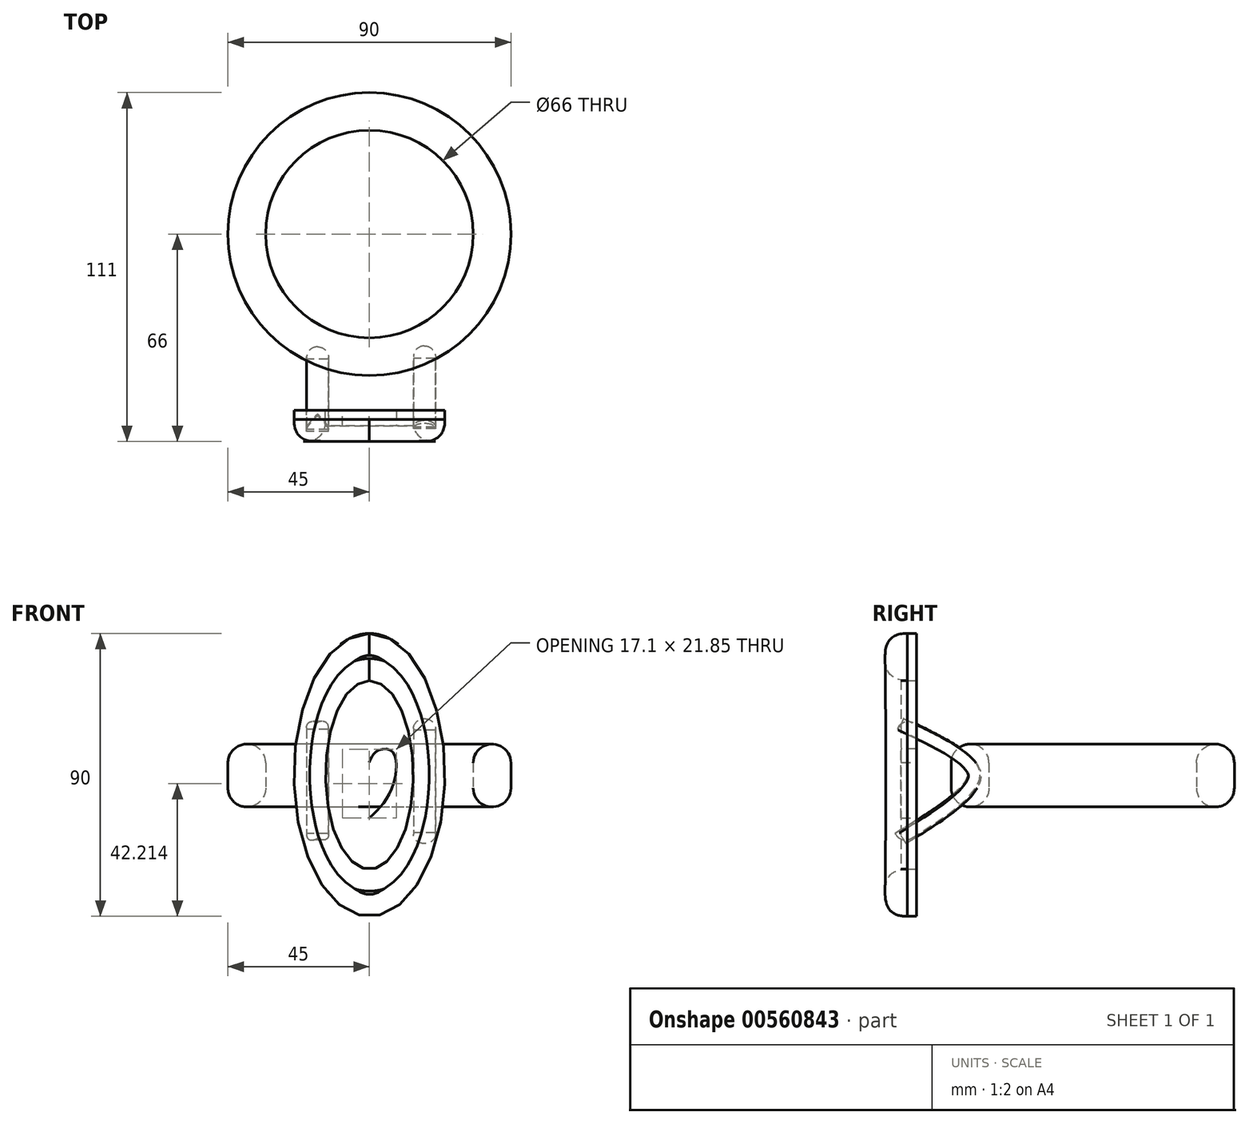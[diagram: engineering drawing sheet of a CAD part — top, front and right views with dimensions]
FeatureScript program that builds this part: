
annotation { "Feature Type Name" : "Feature", "Feature Type Description" : "" }
export const myFeature = defineFeature(function(context is Context, id is Id, definition is map)
    precondition{}
    {
        {
            var Q0;
            Q0=qCreatedBy(makeId("Top.planeOp"),FACE);
            var sketch = newSketch(context, id + "F0", { "sketchPlane" : qUnion([Q0])});
            skCircle(sketch, "E0", {"center": v(0, 0) * mm, "radius": 45 * mm});
            skCircle(sketch, "E1", {"center": v(0, 0) * mm, "radius": 33 * mm});
            skSolve(sketch);
        }
        {
            var Q0;
            Q0=makeQuery(id+"F0.imprint","IMPRINT",FACE,{"disambiguationData":[TD([[makeQuery(id+"F0.imprint","IMPRINT",EDGE,{"derivedFrom":sQuery(id+"F0.wireOp",EDGE,"E0")}),1.0]])]});
            extrude(context, id + "F1", {"entities" : qUnion([Q0]), "depth" : 20 * mm, "offsetDistance" : 25 * mm});
        }
        {
            var Q0;
            Q0=makeQuery(id+"F1.opExtrude","CAP_EDGE",EDGE,{"disambiguationData":[OSD([sQuery(id+"F0.wireOp",EDGE,"E0")])],"isStart":false});
            fillet(context, id + "F2", {"entities" : qUnion([Q0]), "radius" : 6 * mm, "tangentPropagation" : true, "allowEdgeOverflow" : false});
        }
        {
            var Q0;
            Q0=makeQuery(id+"F1.opExtrude","CAP_EDGE",EDGE,{"disambiguationData":[OSD([sQuery(id+"F0.wireOp",EDGE,"E0")])],"isStart":true});
            fillet(context, id + "F3", {"entities" : qUnion([Q0]), "radius" : 6 * mm, "tangentPropagation" : true, "allowEdgeOverflow" : false});
        }
        {
            var Q0;
            Q0=makeQuery(id+"F1.opExtrude","CAP_EDGE",EDGE,{"disambiguationData":[OSD([sQuery(id+"F0.wireOp",EDGE,"E1")])],"isStart":false});
            fillet(context, id + "F4", {"entities" : qUnion([Q0]), "radius" : 6 * mm, "tangentPropagation" : true, "allowEdgeOverflow" : false});
        }
        {
            var Q0;
            Q0=makeQuery(id+"F1.opExtrude","CAP_EDGE",EDGE,{"disambiguationData":[OSD([sQuery(id+"F0.wireOp",EDGE,"E1")])],"isStart":true});
            fillet(context, id + "F5", {"entities" : qUnion([Q0]), "radius" : 6 * mm, "tangentPropagation" : true, "allowEdgeOverflow" : false});
        }
        {
            var Q0;
            Q0=qCreatedBy(makeId("Front.planeOp"),FACE);
            cPlane(context, id + "F6", {"entities" : qUnion([Q0]), "cplaneType" : CPlaneType.OFFSET, "offset" : 56 * mm, "width" : 150 * mm, "height" : 150 * mm});
        }
        {
            var Q0;
            Q0=qCreatedBy(id+"F6.planeOp",FACE);
            var sketch = newSketch(context, id + "F7", { "sketchPlane" : qUnion([Q0])});
            skPoint(sketch, "E2", {"position": v(0, 10.21) * mm});
            skEllipse(sketch, "E3", {"center": v(0, 10.21) * mm, "majorRadius": 45 * mm, "minorRadius": 24 * mm, "majorAxis": v(0, 1)});
            skEllipse(sketch, "E4", {"center": v(0, 10.21) * mm, "majorRadius": 30 * mm, "minorRadius": 14 * mm, "majorAxis": v(0, 1)});
            skFitSpline(sketch, "E5", {"points": [v(0, -3.5) * mm, v(7.14, 5.92) * mm, v(7.33, 17.53) * mm, v(2.27, 17.72) * mm, v(0, 14.16) * mm], "startDerivative": vector(26.78, 25.78) * mm, "endDerivative": vector(-8, -22.31) * mm});
            skFitSpline(sketch, "E6.MirrorCS", {"points": [v(0, -3.5) * mm, v(-7.14, 5.92) * mm, v(-7.33, 17.53) * mm, v(-2.27, 17.72) * mm, v(0, 14.16) * mm], "startDerivative": vector(-26.78, 25.78) * mm, "endDerivative": vector(8, -22.31) * mm});
            skSolve(sketch);
        }
        {
            var Q0;
            Q0=qCreatedBy(makeId("Right.planeOp"),FACE);
            cPlane(context, id + "F8", {"entities" : qUnion([Q0]), "cplaneType" : CPlaneType.OFFSET, "offset" : 14 * mm, "width" : 150 * mm, "height" : 150 * mm});
        }
        {
            var Q0;
            Q0=qCreatedBy(id+"F8.planeOp",FACE);
            var sketch = newSketch(context, id + "F9", { "sketchPlane" : qUnion([Q0])});
            skFitSpline(sketch, "E7", {"points": [v(-60.15, 28.08) * mm, v(-35.58, 10.21) * mm, v(-59.33, -11.64) * mm], "startDerivative": vector(74.5, -34.9) * mm, "endDerivative": vector(-73.74, -45.75) * mm});
            skFitSpline(sketch, "E8.0", {"points": [v(-61.85, 24.46) * mm, v(-60.3, 23.73) * mm, v(-57.22, 22.29) * mm, v(-52.83, 20.14) * mm, v(-48.8, 18.02) * mm, v(-45.3, 15.92) * mm, v(-42.97, 14.23) * mm, v(-41.53, 12.97) * mm, v(-40.7, 12.08) * mm, v(-40.1, 11.3) * mm, v(-39.75, 10.66) * mm, v(-39.62, 10.27) * mm, v(-39.58, 10.02) * mm, v(-39.56, 9.86) * mm, v(-39.57, 9.68) * mm, v(-39.61, 9.38) * mm, v(-39.75, 8.9) * mm, v(-40.11, 8.14) * mm, v(-40.9, 6.91) * mm, v(-42.49, 5.1) * mm, v(-45.23, 2.65) * mm, v(-48.64, 0.06) * mm, v(-52.57, -2.63) * mm, v(-56.87, -5.4) * mm, v(-59.9, -7.3) * mm, v(-61.44, -8.24) * mm]});
            skLineSegment(sketch, "E9", {"start": v(-60.15, 28.08) * mm, "end": v(-61.85, 24.46) * mm});
            skLineSegment(sketch, "E10", {"start": v(-61.44, -8.24) * mm, "end": v(-59.33, -11.64) * mm});
            skSolve(sketch);
        }
        {
            var Q0;
            Q0=makeQuery(id+"F7.imprint","IMPRINT",FACE,{"disambiguationData":[TD([[makeQuery(id+"F7.imprint","IMPRINT",EDGE,{"derivedFrom":sQuery(id+"F7.wireOp",EDGE,"E3")}),1.0]])]});
            extrude(context, id + "F10", {"entities" : qUnion([Q0]), "depth" : 10 * mm, "offsetDistance" : 25 * mm});
        }
        {
            var Q0;
            Q0=makeQuery(id+"F10.opExtrude","CAP_EDGE",EDGE,{"disambiguationData":[OSD([sQuery(id+"F7.wireOp",EDGE,"E4")])],"isStart":false});
            var Q1;
            Q1=makeQuery(id+"F10.opExtrude","CAP_EDGE",EDGE,{"disambiguationData":[OSD([sQuery(id+"F7.wireOp",EDGE,"E3")])],"isStart":false});
            fillet(context, id + "F11", {"entities" : qUnion([Q0, Q1]), "radius" : 7 * mm, "tangentPropagation" : true, "rho" : 0.5, "crossSection" : FilletCrossSection.CONIC, "allowEdgeOverflow" : false});
        }
        {
            var Q0;
            Q0=makeQuery(id+"F9.imprint","IMPRINT",FACE,{"disambiguationData":[TD([[makeQuery(id+"F9.imprint","IMPRINT",EDGE,{"derivedFrom":sQuery(id+"F9.wireOp",EDGE,"E7")}),-1.0]])]});
            extrude(context, id + "F12", {"entities" : qUnion([Q0]), "depth" : 7 * mm, "offsetDistance" : 25 * mm});
        }
        {
            var Q0;
            Q0=qCreatedBy(makeId("Right.planeOp"),FACE);
            cPlane(context, id + "F13", {"entities" : qUnion([Q0]), "cplaneType" : CPlaneType.OFFSET, "offset" : 20 * mm, "oppositeDirection" : true, "width" : 150 * mm, "height" : 150 * mm});
        }
        {
            var Q0;
            Q0=qCreatedBy(id+"F13.planeOp",FACE);
            var sketch = newSketch(context, id + "F14", { "sketchPlane" : qUnion([Q0])});
            skFitSpline(sketch, "E11", {"points": [v(-60.42, 28.37) * mm, v(-35.85, 10.5) * mm, v(-60.74, -11.83) * mm], "startDerivative": vector(74.5, -34.9) * mm, "endDerivative": vector(-73.95, -45.42) * mm});
            skFitSpline(sketch, "E12.0", {"points": [v(-62.12, 24.75) * mm, v(-60.56, 24.02) * mm, v(-57.48, 22.58) * mm, v(-53.05, 20.42) * mm, v(-48.98, 18.28) * mm, v(-45.45, 16.17) * mm, v(-43.1, 14.47) * mm, v(-41.67, 13.2) * mm, v(-40.85, 12.32) * mm, v(-40.3, 11.55) * mm, v(-39.98, 10.93) * mm, v(-39.87, 10.56) * mm, v(-39.84, 10.33) * mm, v(-39.84, 10.12) * mm, v(-39.88, 9.76) * mm, v(-40.1, 9.12) * mm, v(-40.53, 8.3) * mm, v(-41.44, 7) * mm, v(-43.2, 5.09) * mm, v(-46.13, 2.57) * mm, v(-49.72, -0.07) * mm, v(-53.8, -2.8) * mm, v(-58.22, -5.6) * mm, v(-61.29, -7.48) * mm, v(-62.83, -8.43) * mm]});
            skLineSegment(sketch, "E13", {"start": v(-60.42, 28.37) * mm, "end": v(-62.12, 24.75) * mm});
            skLineSegment(sketch, "E14", {"start": v(-62.83, -8.43) * mm, "end": v(-60.74, -11.83) * mm});
            skSolve(sketch);
        }
        {
            var Q0;
            Q0=makeQuery(id+"F14.imprint","IMPRINT",FACE,{"disambiguationData":[TD([[makeQuery(id+"F14.imprint","IMPRINT",EDGE,{"derivedFrom":sQuery(id+"F14.wireOp",EDGE,"E11")}),-1.0]])]});
            extrude(context, id + "F15", {"entities" : qUnion([Q0]), "depth" : 7 * mm, "offsetDistance" : 25 * mm});
        }
        {
            var Q0;
            Q0=makeQuery(id+"F12.opExtrude","CAP_EDGE",EDGE,{"disambiguationData":[OSD([sQuery(id+"F9.wireOp",EDGE,"E7")])],"isStart":false});
            var Q1;
            Q1=makeQuery(id+"F12.opExtrude","CAP_EDGE",EDGE,{"disambiguationData":[OSD([sQuery(id+"F9.wireOp",EDGE,"E7")])],"isStart":true});
            fillet(context, id + "F16", {"entities" : qUnion([Q0, Q1]), "radius" : 3.5 * mm, "tangentPropagation" : true, "allowEdgeOverflow" : false});
        }
        {
            var Q0;
            Q0=makeQuery(id+"F15.opExtrude","CAP_EDGE",EDGE,{"disambiguationData":[OSD([sQuery(id+"F14.wireOp",EDGE,"E11")])],"isStart":true});
            var Q1;
            Q1=makeQuery(id+"F15.opExtrude","SWEPT_FACE",FACE,{"disambiguationData":[OSD([sQuery(id+"F14.wireOp",EDGE,"E11")])]});
            fillet(context, id + "F17", {"entities" : qUnion([Q0, Q1]), "radius" : 3.5 * mm, "tangentPropagation" : true, "allowEdgeOverflow" : false});
        }
        {
            var Q0;
            Q0=makeQuery(id+"F7.imprint","IMPRINT",FACE,{"disambiguationData":[TD([[makeQuery(id+"F7.imprint","IMPRINT",EDGE,{"derivedFrom":sQuery(id+"F7.wireOp",EDGE,"E4")}),1.0]])]});
            extrude(context, id + "F18", {"entities" : qUnion([Q0]), "depth" : 5 * mm, "offsetDistance" : 25 * mm});
        }
    });
